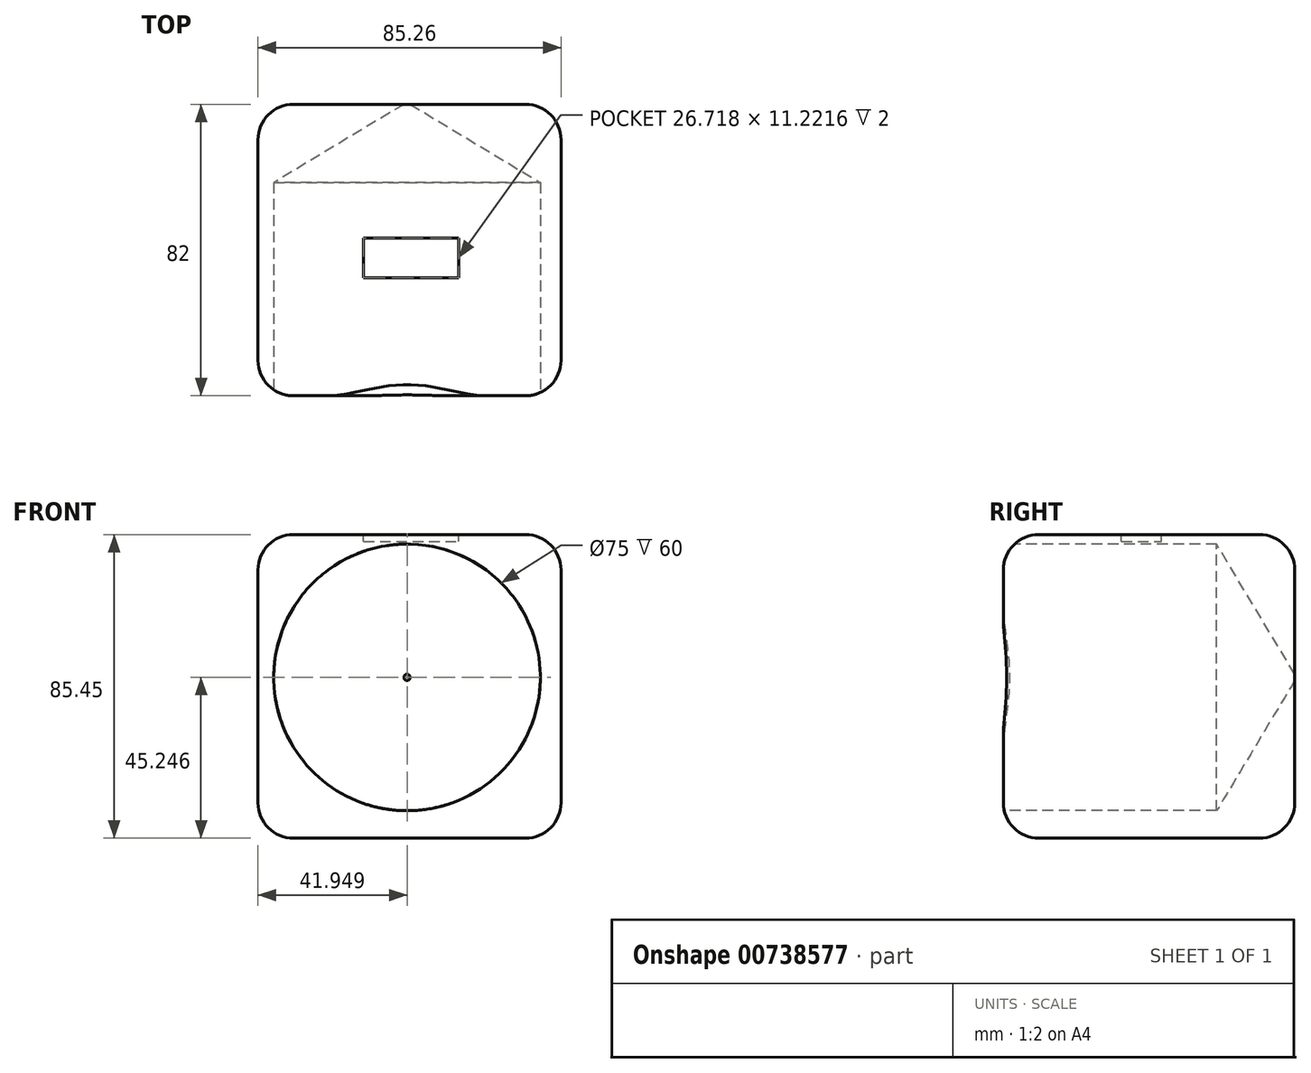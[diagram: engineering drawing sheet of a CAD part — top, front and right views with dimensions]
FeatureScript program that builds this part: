
annotation { "Feature Type Name" : "Feature", "Feature Type Description" : "" }
export const myFeature = defineFeature(function(context is Context, id is Id, definition is map)
    precondition{}
    {
        {
            var Q0;
            Q0=qCreatedBy(makeId("Front.planeOp"),FACE);
            var sketch = newSketch(context, id + "F0", { "sketchPlane" : qUnion([Q0])});
            skLineSegment(sketch, "E0.bottom", {"start": v(-33.2, -15.63) * mm, "end": v(52.05, -15.63) * mm});
            skLineSegment(sketch, "E0.top", {"start": v(-33.2, 69.82) * mm, "end": v(52.05, 69.82) * mm});
            skLineSegment(sketch, "E0.left", {"start": v(-33.2, -15.63) * mm, "end": v(-33.2, 69.82) * mm});
            skLineSegment(sketch, "E0.right", {"start": v(52.05, -15.63) * mm, "end": v(52.05, 69.82) * mm});
            skSolve(sketch);
        }
        {
            var Q0;
            Q0=qSketchRegion(id+"F0",true);
            var Q1;
            Q1=makeQuery(id+"F0.imprint","IMPRINT",FACE,{"disambiguationData":[TD([[makeQuery(id+"F0.imprint","IMPRINT",EDGE,{"derivedFrom":sQuery(id+"F0.wireOp",EDGE,"E0.bottom")}),1.0]])]});
            extrude(context, id + "F1", {"entities" : qUnion([Q0, Q1]), "depth" : 82 * mm});
        }
        {
            var Q0;
            Q0=makeQuery(id+"F1.opExtrude","CAP_FACE",FACE,{"disambiguationData":[OSD([sQuery(id+"F0.wireOp",EDGE,"E0.bottom"),sQuery(id+"F0.wireOp",EDGE,"E0.top"),sQuery(id+"F0.wireOp",EDGE,"E0.left"),sQuery(id+"F0.wireOp",EDGE,"E0.right")])],"isStart":false});
            var sketch = newSketch(context, id + "F2", { "sketchPlane" : qUnion([Q0])});
            skCircle(sketch, "E1", {"center": v(8.74, 29.62) * mm, "radius": 34.8 * mm});
            skSolve(sketch);
        }
        {
            var Q0;
            Q0=sQuery(id+"F2.wireOp",VERTEX,"E1.center");
            var Q1;
            Q1=makeQuery(id+"F1.opExtrude","SWEPT_BODY",BODY,{"disambiguationData":[OSD([sQuery(id+"F0.wireOp",EDGE,"E0.bottom"),sQuery(id+"F0.wireOp",EDGE,"E0.top"),sQuery(id+"F0.wireOp",EDGE,"E0.left"),sQuery(id+"F0.wireOp",EDGE,"E0.right")])]});
            hole(context, id + "F3", {"style" : HoleStyle.SIMPLE, "endStyle" : HoleEndStyle.BLIND, "holeDiameter" : 75 * mm, "holeDepth" : 60 * mm, "tappedDepth" : 12 * mm, "tapClearance" : 3, "locations" : qUnion([Q0]), "scope" : qUnion([Q1])});
        }
        {
            var Q0;
            Q0=makeQuery(id+"F1.opExtrude","SWEPT_EDGE",EDGE,{"disambiguationData":[OSD([sQuery(id+"F0.wireOp",EDGE,"E0.top"),sQuery(id+"F0.wireOp",EDGE,"E0.right")])]});
            fillet(context, id + "F4", {"entities" : qUnion([Q0]), "radius" : 10 * mm, "tangentPropagation" : true, "allowEdgeOverflow" : false});
        }
        {
            var Q0;
            Q0=makeQuery(id+"F1.opExtrude","SWEPT_EDGE",EDGE,{"disambiguationData":[OSD([sQuery(id+"F0.wireOp",EDGE,"E0.top"),sQuery(id+"F0.wireOp",EDGE,"E0.left")])]});
            fillet(context, id + "F5", {"entities" : qUnion([Q0]), "radius" : 10 * mm, "tangentPropagation" : true, "allowEdgeOverflow" : false});
        }
        {
            var Q0;
            Q0=makeQuery(id+"F1.opExtrude","SWEPT_EDGE",EDGE,{"disambiguationData":[OSD([sQuery(id+"F0.wireOp",EDGE,"E0.bottom"),sQuery(id+"F0.wireOp",EDGE,"E0.right")])]});
            fillet(context, id + "F6", {"entities" : qUnion([Q0]), "radius" : 10 * mm, "tangentPropagation" : true, "allowEdgeOverflow" : false});
        }
        {
            var Q0;
            Q0=makeQuery(id+"F1.opExtrude","CAP_EDGE",EDGE,{"disambiguationData":[OSD([sQuery(id+"F0.wireOp",EDGE,"E0.bottom")])],"isStart":true});
            fillet(context, id + "F7", {"entities" : qUnion([Q0]), "radius" : 10 * mm, "tangentPropagation" : true, "allowEdgeOverflow" : false});
        }
        {
            var Q0;
            Q0=makeQuery(id+"F1.opExtrude","SWEPT_EDGE",EDGE,{"disambiguationData":[OSD([sQuery(id+"F0.wireOp",EDGE,"E0.bottom"),sQuery(id+"F0.wireOp",EDGE,"E0.left")])]});
            var Q1;
            Q1=makeQuery(id+"F1.opExtrude","CAP_EDGE",EDGE,{"disambiguationData":[OSD([sQuery(id+"F0.wireOp",EDGE,"E0.top")])],"isStart":false});
            fillet(context, id + "F8", {"entities" : qUnion([Q0, Q1]), "radius" : 10 * mm, "tangentPropagation" : true, "allowEdgeOverflow" : false});
        }
        {
            var Q0;
            Q0=makeQuery(id+"F1.opExtrude","SWEPT_FACE",FACE,{"disambiguationData":[OSD([sQuery(id+"F0.wireOp",EDGE,"E0.top")])]});
            var sketch = newSketch(context, id + "F9", { "sketchPlane" : qUnion([Q0])});
            skLineSegment(sketch, "E2.bottom", {"start": v(-3.47, -48.79) * mm, "end": v(23.24, -48.79) * mm});
            skLineSegment(sketch, "E2.top", {"start": v(-3.47, -37.57) * mm, "end": v(23.24, -37.57) * mm});
            skLineSegment(sketch, "E2.left", {"start": v(-3.47, -48.79) * mm, "end": v(-3.47, -37.57) * mm});
            skLineSegment(sketch, "E2.right", {"start": v(23.24, -48.79) * mm, "end": v(23.24, -37.57) * mm});
            skSolve(sketch);
        }
        {
            var Q0;
            Q0=makeQuery(id+"F9.imprint","IMPRINT",FACE,{"disambiguationData":[TD([[makeQuery(id+"F9.imprint","IMPRINT",EDGE,{"derivedFrom":sQuery(id+"F9.wireOp",EDGE,"E2.bottom")}),1.0]])]});
            extrude(context, id + "F10", {"entities" : qUnion([Q0]), "operationType" : NewBodyOperationType.REMOVE, "oppositeDirection" : true, "depth" : 2 * mm});
        }
    });
